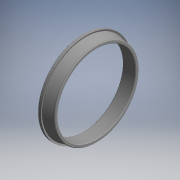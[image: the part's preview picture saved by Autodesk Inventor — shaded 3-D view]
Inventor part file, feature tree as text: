
AUTODESK INVENTOR PART (.ipt)
format: ipt  version: 2017.3 (Build 213256000, 256)  size: 134,144 bytes
history: native  units: mm (DEFAULTED — no unit token found)
features: other x7, revolve x1, sketch x1
ambient origin geometry x8: Origin, YZ Plane, XZ Plane, XY Plane, X Axis, Y Axis, Z Axis, Center Point
bodies: Solid1 (feature_tree)
feature tree (9):
  revolve  "Revolution1"  [1 undecoded]
  other  "inner_ring_XY"
  other  "inner_ring_YZ"
  other  "inner_ring_ZX"
  other  "inner_ring_X"
  other  "inner_ring_Y"
  other  "inner_ring_Z"
  other  "inner_ring_Center"
  sketch  "Sketch_1"  dims[d0=360.0deg]
note: 1 required parameter value undecoded (feature->parameter linkage not recoverable at this tier; creation-order binding heuristic only, values carry confidence <= 0.55)
